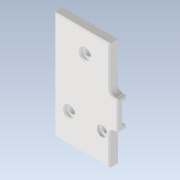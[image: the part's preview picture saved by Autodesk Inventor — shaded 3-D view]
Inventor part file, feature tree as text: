
AUTODESK INVENTOR PART (.ipt)
format: ipt  version: 2022.1 (Build 261234020, 234B)  size: 219,136 bytes
history: native  units: mm
features: reference x13, direct_edit x4, sketch x4, move_body x4, extrude x3, projected_geometry x3, other x3, chamfer x2, hole x1, fillet x1
ambient origin geometry x8: Origin, YZ Plane, XZ Plane, XY Plane, X Axis, Y Axis, Z Axis, Center Point
bodies: Volumenkörper1 (feature_tree)
feature tree (38):
  extrude  "Extrusion1"  Depth=3.0mm TaperAngle=0.0deg
  extrude  "Extrusion2"  TaperAngle=0.0deg  [1 undecoded]
  hole  "Bohrung1"  [1 undecoded]
  direct_edit  "Direktbearbeitung1"
  direct_edit  "Direktbearbeitung2"
  extrude  "Extrusion3"  Depth=2.0mm
  direct_edit  "Direktbearbeitung3"
  direct_edit  "Direktbearbeitung5"
  fillet  "Rundung1"  Radius=1.6mm
  chamfer  "Fase2"  Distance=0.2mm
  chamfer  "Fase3"  [1 undecoded]
  sketch  "Skizze1"  dims[d0=0.4mm d1=3.0mm d2=0.0mm]
  reference  "Referenz1"
  reference  "Referenz2"
  reference  "Referenz3"
  reference  "Referenz4"
  reference  "Referenz5"
  reference  "Referenz6"
  reference  "Referenz7"
  reference  "Referenz8"
  reference  "Referenz9"
  reference  "Referenz10"
  reference  "Referenz11"
  reference  "Referenz12"
  reference  "Referenz13"
  sketch  "Skizze2"  dims[d3=1.0mm d4=0.0mm]
  projected_geometry  "Projizierte Kontur1"
  sketch  "Skizze3"  dims[d5=2.0mm d6=6.0mm d7=3.6mm d8=1.2mm d9=90.0deg d10=8.0mm d11=20.594885mm d15=0.0mm d16=0.0mm d17=-0.2mm]
  projected_geometry  "Projizierte Kontur2"
  sketch  "Skizze4"  dims[d18=0.0mm d19=0.0mm d20=1.41mm d21=4.597504mm d22=1.21mm d23=1.6mm d24=0.0mm d25=0.0mm d26=0.0mm d27=0.2mm d31=0.0mm d32=0.0mm d33=-0.6mm d34=0.5mm d35=0.4mm d36=2.0mm d37=45.0deg d38=0.4mm d39=2.0mm d40=45.0deg]
  projected_geometry  "Projizierte Kontur3"
  other  "<userpath>\Desktop\RAMA_SBNG\z_Endstop\Baugruppe1.iam"
  other  "Baugruppe1.iam"
  other  "housing:1"
  move_body  "Verschieben1"
  move_body  "Verschieben2"
  move_body  "Verschieben3"
  move_body  "Verschieben5"
note: 3 required parameter values undecoded (feature->parameter linkage not recoverable at this tier; creation-order binding heuristic only, values carry confidence <= 0.55)
